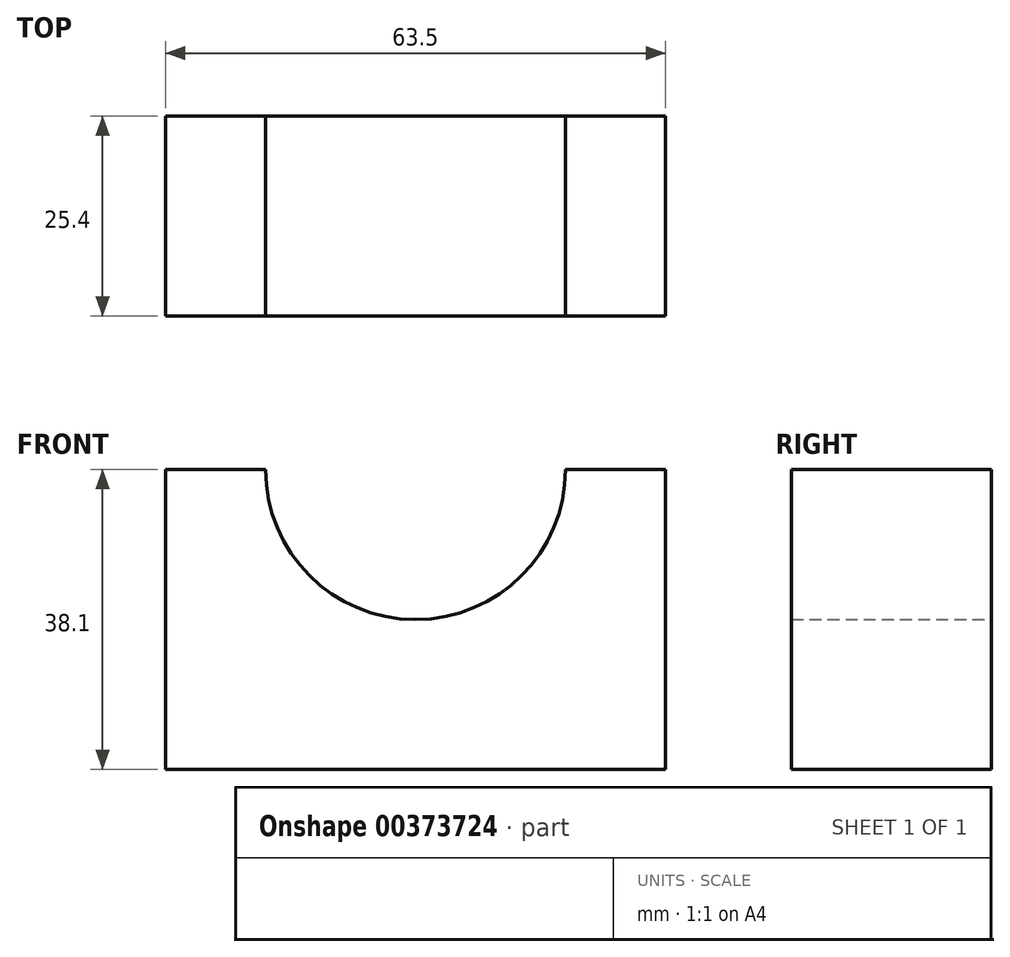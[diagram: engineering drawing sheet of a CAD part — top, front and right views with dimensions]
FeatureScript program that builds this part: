
annotation { "Feature Type Name" : "Feature", "Feature Type Description" : "" }
export const myFeature = defineFeature(function(context is Context, id is Id, definition is map)
    precondition{}
    {
        {
            var Q0;
            Q0=qCreatedBy(makeId("Right.planeOp"),FACE);
            var sketch = newSketch(context, id + "F0", { "sketchPlane" : qUnion([Q0])});
            skLineSegment(sketch, "E0.bottom", {"start": v(0, 0) * mm, "end": v(25.4, 0) * mm});
            skLineSegment(sketch, "E0.top", {"start": v(0, 38.1) * mm, "end": v(25.4, 38.1) * mm});
            skLineSegment(sketch, "E0.left", {"start": v(0, 0) * mm, "end": v(0, 38.1) * mm});
            skLineSegment(sketch, "E0.right", {"start": v(25.4, 0) * mm, "end": v(25.4, 38.1) * mm});
            skSolve(sketch);
        }
        {
            var Q0;
            Q0 = qSketchRegion(id + "F0", true);
            extrude(context, id + "F1", {"entities" : qUnion([Q0]), "depth" : 63.5 * mm});
        }
        {
            var Q0;
            Q0=makeQuery(id+"F1.opExtrude","SWEPT_FACE",FACE,{"disambiguationData":[OSD([sQuery(id+"F0.wireOp",EDGE,"E0.right")])]});
            var sketch = newSketch(context, id + "F2", { "sketchPlane" : qUnion([Q0])});
            skCircle(sketch, "E1", {"center": v(-31.75, 38.1) * mm, "radius": 19.05 * mm});
            skSolve(sketch);
        }
        {
            var Q0;
            Q0 = qSketchRegion(id + "F2", true);
            extrude(context, id + "F3", {"entities" : qUnion([Q0]), "operationType" : NewBodyOperationType.REMOVE, "oppositeDirection" : true, "depth" : 25.4 * mm});
        }
    });
